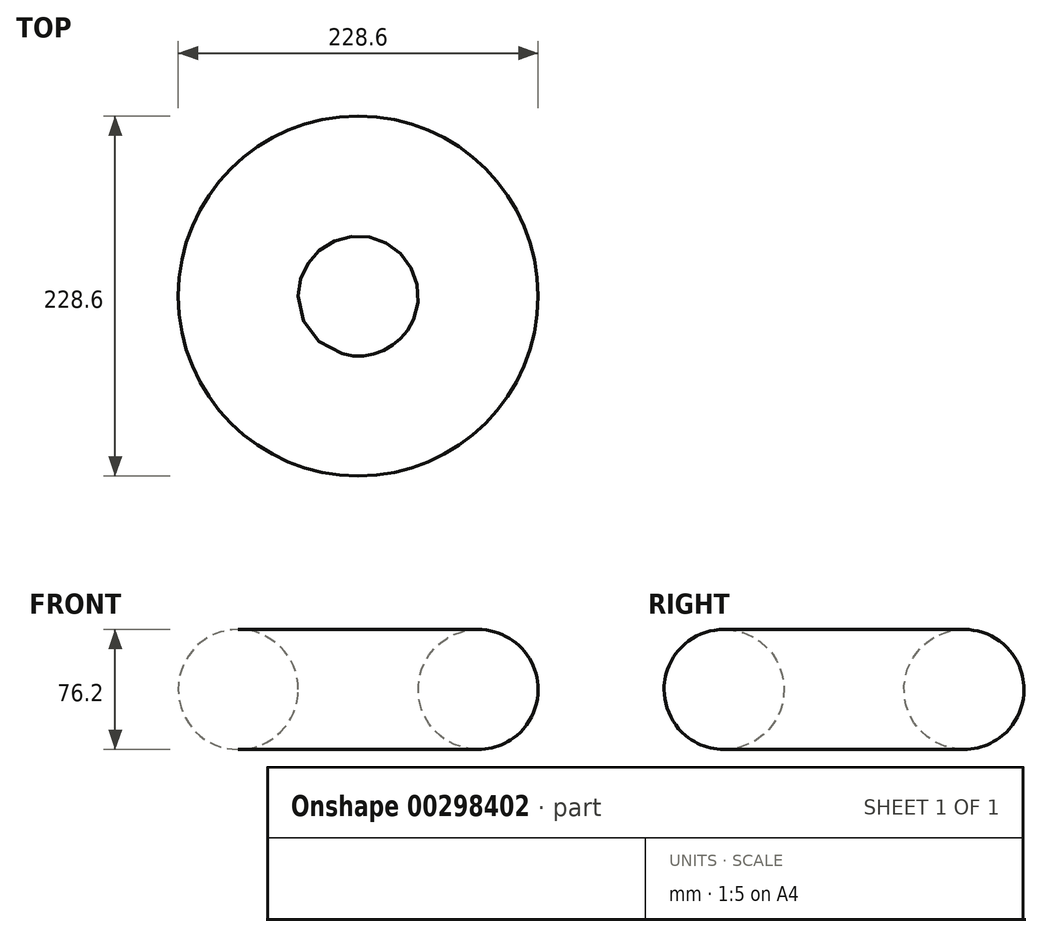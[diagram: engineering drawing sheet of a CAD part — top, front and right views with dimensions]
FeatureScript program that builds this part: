
annotation { "Feature Type Name" : "Feature", "Feature Type Description" : "" }
export const myFeature = defineFeature(function(context is Context, id is Id, definition is map)
    precondition{}
    {
        {
            var Q0;
            Q0=qCreatedBy(makeId("Top.planeOp"),FACE);
            var sketch = newSketch(context, id + "F0", { "sketchPlane" : qUnion([Q0])});
            skCircle(sketch, "E0", {"center": v(0, 0) * mm, "radius": 38.1 * mm});
            skSolve(sketch);
        }
        {
            var Q0;
            Q0=qCreatedBy(makeId("Right.planeOp"),FACE);
            var sketch = newSketch(context, id + "F1", { "sketchPlane" : qUnion([Q0])});
            skCircle(sketch, "E1", {"center": v(-76.2, 0) * mm, "radius": 38.1 * mm});
            skSolve(sketch);
        }
        {
            var Q0;
            Q0=makeQuery(id+"F1.imprint","IMPRINT",FACE,{"disambiguationData":[TD([[makeQuery(id+"F1.imprint","IMPRINT",EDGE,{"derivedFrom":sQuery(id+"F1.wireOp",EDGE,"E1")}),1.0]])]});
            var Q1;
            Q1=sQuery(id+"F0.wireOp",EDGE,"E0");
            revolve(context, id + "F2", {"entities" : qUnion([Q0]), "axis" : qUnion([Q1]), "revolveType" : RevolveType.FULL});
        }
    });
